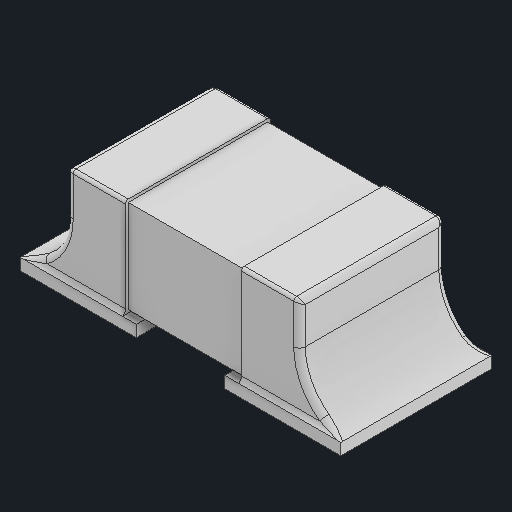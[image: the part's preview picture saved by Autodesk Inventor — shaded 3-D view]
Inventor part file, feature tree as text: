
AUTODESK INVENTOR PART (.ipt)
format: ipt  version: 2023 (Build 270158000, 158)  size: 150,016 bytes
history: native  units: in
note: dims shown in document units (in); Inventor stores cm internally (conversion verified against a paired STEP export)
features: fillet x1
ambient origin geometry x8: Origin, YZ Plane, XZ Plane, XY Plane, X Axis, Y Axis, Z Axis, Center Point
bodies: Solid1 (feature_tree)
feature tree (1):
  fillet  "Fillet8"  [1 undecoded]
note: 1 required parameter value undecoded (feature->parameter linkage not recoverable at this tier; creation-order binding heuristic only, values carry confidence <= 0.55)
